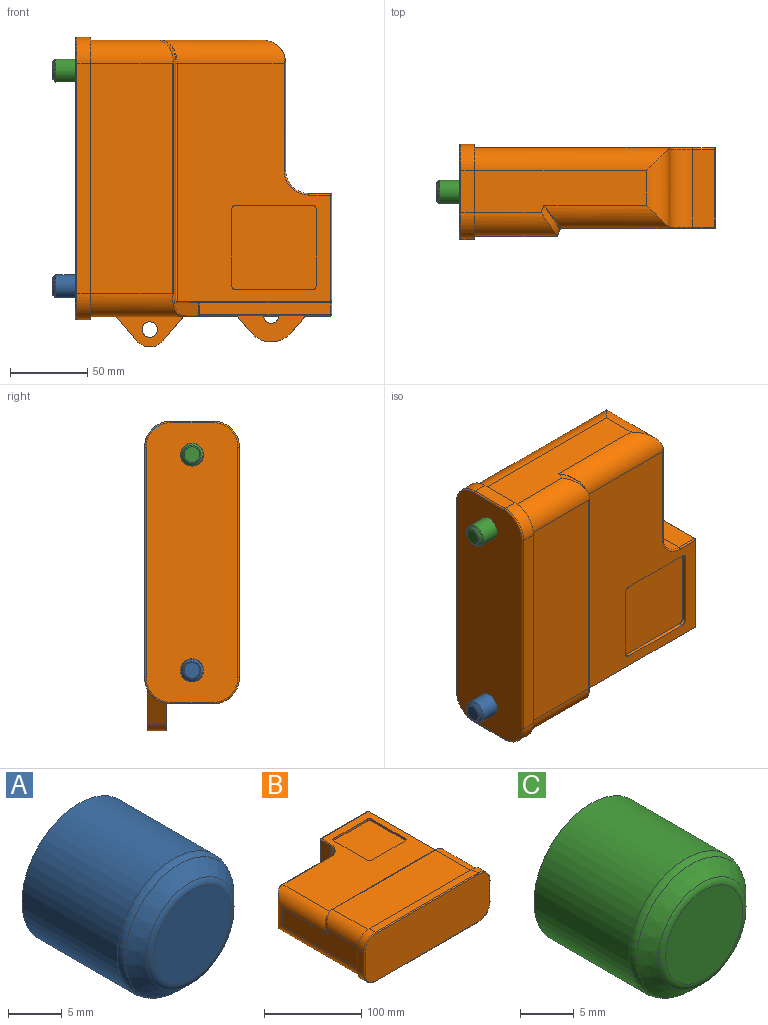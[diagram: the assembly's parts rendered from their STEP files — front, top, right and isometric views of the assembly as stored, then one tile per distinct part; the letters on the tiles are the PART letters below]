
ASSEMBLY  parts=3 mates=2
PART A: 6 faces, bbox 16.2x15x16.2 mm
  f0: cylinder r=7.5mm len=15mm, axis (0,-1,0), area 593.1mm2, adj f2,f4
  f1: plane 10.17x10.17mm, normal (0,-1,0), area 81.3mm2, adj f5
  f2: plane 15x15mm, normal (0,1,0), area 176.7mm2, adj f0
  f3: cone r=5.5mm half-angle=45deg, axis (0,1,0), area 81.7mm2, adj f4,f5
  f4: torus R=6.5mm, axis (0,-1,0), area 36.5mm2, adj f0,f3
  f5: torus R=5.09mm, axis (0,-1,0), area 26.9mm2, adj f1,f3
PART B: 131 faces, bbox 202.6x166.6x64.4 mm
  f0: cylinder r=15mm len=16.23mm, axis (0,1,0), area 221.2mm2, adj f6,f64,f67,f76
  f1: cylinder r=15mm len=95.05mm, axis (0,1,0), area 932.7mm2, adj f6,f7,f29,f61,f65,f67,f78,f81
  f2: plane 154.56x99.36mm, normal (0,0,1), area 9823.6mm2, adj f9,f16,f31,f32,f33,f34,f35,f36
  f3: plane 77.56x50.5mm, normal (0,1,0), area 3498.3mm2, adj f49,f50,f55,f59,f60,f63,f64
  f4: plane 149.5x52.92mm, normal (0,0,1), area 7911.7mm2, adj f13,f20,f29,f47
  f5: plane 111.5x27.5mm, normal (-1,0,0), area 2728.9mm2, adj f13,f14,f15,f16,f17,f29
  f6: plane 184.06x155.5mm, normal (0,0,-1), area 23247.9mm2, adj f0,f1,f15,f29,f43,f46,f51,f60
  f7: plane 68.03x27.5mm, normal (1,0,0), area 1733.1mm2, adj f1,f20,f29,f57
  f8: plane 163.5x43.68mm, normal (0,0.94,0.34), area 936.6mm2, adj f14,f47,f48,f52,f53,f57,f61,f62
  f9: plane 98.99x39mm, normal (1,0,0), area 3584mm2, adj f2,f53,f54,f55
  f10: plane 84.8x7.56mm, normal (0,0,1), area 640.7mm2, adj f54,f62,f63,f67
  f11: plane 69.5x50.5mm, normal (0,1,0), area 3509.8mm2, adj f17,f18,f40,f43
  f12: plane 50.5x14mm, normal (-1,0,0), area 707mm2, adj f18,f42,f50,f51
  f13: cylinder r=15mm len=53.49mm, axis (0,1,0), area 1172.6mm2, adj f4,f5,f14,f29,f47
  f14: cylinder r=15mm len=19.88mm, axis (0,0.34,-0.94), area 114mm2, adj f5,f8,f13,f44,f47
  f15: cylinder r=15mm len=126.21mm, axis (0,-1,0), area 2850.5mm2, adj f5,f6,f17,f29,f43
  f16: cylinder r=15mm len=81.27mm, axis (0,-1,0), area 1623.6mm2, adj f2,f5,f17,f40,f44
  f17: cylinder r=15mm len=51.91mm, axis (0,0,-1), area 976.9mm2, adj f5,f11,f15,f16,f40,f43
  f18: cylinder r=15mm len=50.5mm, axis (0,0,1), area 1189.9mm2, adj f11,f12,f41,f46
  f19: cylinder r=15mm len=10mm, axis (0,1,0), area 83.1mm2, adj f67,f79
  f20: cylinder r=15mm len=58.02mm, axis (0,-1,0), area 1290.6mm2, adj f4,f7,f29,f52
  f21: cylinder r=17mm len=17mm, axis (0,1,0), area 240.3mm2, adj f22,f28,f29,f75
  f22: plane 27.5x9mm, normal (-1,0,0), area 247.5mm2, adj f21,f23,f29,f73
  f23: cylinder r=17mm len=17mm, axis (0,1,0), area 240.3mm2, adj f22,f24,f29,f71
  f24: plane 149.5x9mm, normal (0,0,-1), area 1345.5mm2, adj f23,f25,f29,f69
  f25: cylinder r=17mm len=17mm, axis (0,1,0), area 240.3mm2, adj f24,f26,f29,f68
  f26: plane 27.5x9mm, normal (1,0,0), area 247.5mm2, adj f25,f27,f29,f70
  f27: cylinder r=17mm len=17mm, axis (0,1,0), area 240.3mm2, adj f26,f28,f29,f72
  f28: plane 149.5x9mm, normal (0,0,1), area 1345.5mm2, adj f21,f27,f29,f74
  f29: plane 183.5x61.5mm, normal (0,1,0), area 909.1mm2, adj f1,f4,f5,f6,f7,f13,f15,f20
  f30: plane 181.5x59.5mm, normal (0,-1,0), area 10579.5mm2, adj f68,f69,f70,f71,f72,f73,f74,f75
  f31: plane 49x2.5mm, normal (0,-1,0), area 122.5mm2, adj f2,f32,f38,f39
  f32: cylinder r=3mm len=3mm, axis (0,0,1), area 11.8mm2, adj f2,f31,f33,f39
  f33: plane 49x2.5mm, normal (1,0,0), area 122.5mm2, adj f2,f32,f34,f39
  f34: cylinder r=3mm len=3mm, axis (0,0,1), area 11.8mm2, adj f2,f33,f35,f39
  f35: plane 49x2.5mm, normal (0,1,0), area 122.5mm2, adj f2,f34,f36,f39
  f36: cylinder r=3mm len=3mm, axis (0,0,1), area 11.8mm2, adj f2,f35,f37,f39
  f37: plane 49x2.5mm, normal (-1,0,0), area 122.5mm2, adj f2,f36,f38,f39
  f38: cylinder r=3mm len=3mm, axis (0,0,1), area 11.8mm2, adj f2,f31,f37,f39
  f39: plane 55x55mm, normal (0,0,1), area 3017.3mm2, adj f31,f32,f33,f34,f35,f36,f37,f38
  f40: cylinder r=1mm len=72.45mm, axis (-1,0,0), area 111.5mm2, adj f2,f11,f16,f17,f41
  f41: torus R=16mm, axis (0,0,1), area 37.9mm2, adj f2,f18,f40,f42
  f42: cylinder r=1mm len=14mm, axis (0,-1,0), area 22mm2, adj f2,f12,f41,f45
  f43: cylinder r=1mm len=72.45mm, axis (1,0,0), area 111.5mm2, adj f6,f11,f15,f17,f46
  f44: bspline ~15.66x15.49mm, area 19.3mm2, adj f14,f16,f48
  f45: sphere r=1mm, area 1.6mm2, adj f42,f49,f50
  f46: torus R=16mm, axis (0,0,-1), area 37.9mm2, adj f6,f18,f43,f51
  f47: cylinder r=1mm len=151.82mm, axis (-1,0,0), area 184.1mm2, adj f4,f8,f13,f14,f52
  f48: cylinder r=1mm len=155.5mm, axis (1,0,0), area 189.3mm2, adj f2,f8,f44,f53
  f49: cylinder r=1mm len=69mm, axis (-1,0,0), area 107.8mm2, adj f2,f3,f45,f55
  f50: cylinder r=1mm len=50.5mm, axis (0,0,1), area 79.3mm2, adj f3,f12,f45,f56
  f51: cylinder r=1mm len=14mm, axis (0,1,0), area 22mm2, adj f6,f12,f46,f56
  f52: bspline ~15.65x15.01mm, area 31.9mm2, adj f8,f20,f47,f57
  f53: cylinder r=1mm len=40.34mm, axis (0,0.34,-0.94), area 65.9mm2, adj f2,f8,f9,f48,f58
  f54: cylinder r=1mm len=84.8mm, axis (0,-1,0), area 133.2mm2, adj f9,f10,f58,f59
  f55: cylinder r=1mm len=39mm, axis (0,0,1), area 60.7mm2, adj f3,f9,f49,f59
  f56: sphere r=1mm, area 1.6mm2, adj f50,f51,f60
  f57: cylinder r=1mm len=27.84mm, axis (0,-0.34,0.94), area 46mm2, adj f7,f8,f52,f61
  f58: sphere r=1mm, area 1.2mm2, adj f53,f54,f62
  f59: torus R=2mm, axis (0,1,0), area 3.4mm2, adj f3,f54,f55,f63
  f60: cylinder r=1mm len=64mm, axis (1,0,0), area 100.5mm2, adj f3,f6,f56,f64
  f61: bspline ~7.44x3.46mm, area 3.9mm2, adj f1,f8,f57,f65
  f62: cylinder r=1mm len=7.83mm, axis (1,0,0), area 9.4mm2, adj f8,f10,f58,f65
  f63: cylinder r=1mm len=7.56mm, axis (-1,0,0), area 11.9mm2, adj f3,f10,f59,f66
  f64: torus R=14mm, axis (0,1,0), area 30.3mm2, adj f0,f3,f60,f66
  f65: bspline ~2.38x2.07mm, area 2.9mm2, adj f1,f61,f62,f67
  f66: sphere r=1mm, area 1.8mm2, adj f63,f64,f67
  f67: cylinder r=1mm len=84.8mm, axis (0,1,0), area 128mm2, adj f0,f1,f10,f19,f65,f66,f76,f78
  f68: torus R=16mm, axis (0,-1,0), area 41mm2, adj f25,f30,f69,f70
  f69: cylinder r=1mm len=149.5mm, axis (-1,0,0), area 234.8mm2, adj f24,f30,f68,f71
  f70: cylinder r=1mm len=27.5mm, axis (0,0,-1), area 43.2mm2, adj f26,f30,f68,f72
  f71: torus R=16mm, axis (0,-1,0), area 41mm2, adj f23,f30,f69,f73
  f72: torus R=16mm, axis (0,-1,0), area 41mm2, adj f27,f30,f70,f74
  f73: cylinder r=1mm len=27.5mm, axis (0,0,1), area 43.2mm2, adj f22,f30,f71,f75
  f74: cylinder r=1mm len=149.5mm, axis (1,0,0), area 234.8mm2, adj f28,f30,f72,f75
  f75: torus R=16mm, axis (0,-1,0), area 41mm2, adj f21,f30,f73,f74
  f76: plane 25.37x21.39mm, normal (0.64,0.76,0), area 223.6mm2, adj f0,f6,f67,f77,f80
  f77: cylinder r=17.09mm len=26.15mm, axis (0,0,-1), area 357.2mm2, adj f6,f76,f78,f80
  f78: plane 25.37x21.39mm, normal (0.64,-0.76,0), area 223.6mm2, adj f1,f6,f67,f77,f80
  f79: cylinder r=5mm len=12mm, axis (0,0,-1), area 269.1mm2, adj f6,f19,f67,f80
  f80: plane 44.39x16.91mm, normal (0,0,1), area 454.9mm2, adj f67,f76,f77,f78,f79
  f81: plane 30.56x25.74mm, normal (0.64,-0.76,0), area 306.9mm2, adj f1,f6,f83,f85
  f82: plane 30.56x25.74mm, normal (0.64,0.76,0), area 306.9mm2, adj f1,f6,f83,f85
  f83: cylinder r=11.25mm len=17.2mm, axis (0,0,-1), area 235mm2, adj f6,f81,f82,f85
  f84: cylinder r=5mm len=12mm, axis (0,0,-1), area 377mm2, adj f6,f85
  f85: plane 43.92x19.87mm, normal (0,0,1), area 454.1mm2, adj f1,f81,f82,f83,f84
  f86: plane 169.5x47.5mm, normal (0,1,0), area 7965.4mm2, adj f94,f95,f96,f97,f103,f105,f108,f109
  f87: cylinder r=20mm len=42.5mm, axis (0,0,1), area 1309.9mm2, adj f88,f93,f96,f101,f102,f111
  f88: plane 65x62.5mm, normal (0,0,-1), area 3996.1mm2, adj f87,f89,f99,f102,f110,f111,f112,f113
  f89: plane 66.61x42.5mm, normal (0,-1,0), area 2446.6mm2, adj f88,f91,f92,f96,f99,f100,f102,f108
  f90: plane 39.07x14.24mm, normal (0,-0.94,-0.34), area 155.2mm2, adj f97,f108,f109,f118,f121
  f91: plane 5.5x2.19mm, normal (0,0,-1), area 3.8mm2, adj f89,f102,f110
  f92: plane 5.5x2.19mm, normal (0,0,-1), area 3.8mm2, adj f89,f99,f115
  f93: plane 149.87x75.69mm, normal (0,0,-1), area 7653.6mm2, adj f87,f99,f101,f106,f111,f112,f113,f114
  f94: plane 149.5x55.12mm, normal (0,0,-1), area 8240.5mm2, adj f86,f98,f103,f109
  f95: plane 116.5x27.5mm, normal (1,0,0), area 2866.4mm2, adj f86,f103,f104,f105,f106,f107
  f96: plane 175.83x156.5mm, normal (0,0,1), area 22040.2mm2, adj f86,f87,f89,f101,f102,f105,f108,f122
  f97: plane 68.77x27.5mm, normal (-1,0,0), area 1753.5mm2, adj f86,f90,f108,f109
  f98: plane 153.97x1.05mm, normal (0,-0.94,-0.34), area 170.8mm2, adj f94,f104,f109,f117
  f99: plane 93.17x34mm, normal (-1,0,0), area 2806mm2, adj f88,f89,f92,f93,f114,f115,f118,f119
  f100: plane 80.8x0.61mm, normal (0,0,-1), area 49.6mm2, adj f89,f108,f119,f121
  f101: plane 69.5x42.5mm, normal (0,-1,0), area 2953.8mm2, adj f87,f93,f96,f107
  f102: plane 42.5x10mm, normal (1,0,0), area 405.5mm2, adj f87,f88,f89,f91,f96,f110
  f103: cylinder r=10mm len=55.12mm, axis (0,1,0), area 825.9mm2, adj f86,f94,f95,f104
  f104: cylinder r=10mm len=15mm, axis (0,0.34,-0.94), area 41.6mm2, adj f95,f98,f103,f116
  f105: cylinder r=10mm len=126.5mm, axis (0,-1,0), area 1930mm2, adj f86,f95,f96,f107
  f106: cylinder r=10mm len=76.56mm, axis (0,-1,0), area 1033.5mm2, adj f93,f95,f107,f116
  f107: cylinder r=10mm len=42.5mm, axis (0,0,-1), area 553.4mm2, adj f95,f101,f105,f106
  f108: cylinder r=10mm len=156.5mm, axis (0,1,0), area 1098.7mm2, adj f86,f89,f90,f96,f97,f100,f121,f122
  f109: cylinder r=10mm len=58.76mm, axis (0,-1,0), area 886.6mm2, adj f86,f90,f94,f97,f98,f117,f118
  f110: cylinder r=8mm len=5.5mm, axis (0,0,1), area 15.2mm2, adj f88,f89,f91,f102
  f111: plane 37.32x2.5mm, normal (-1,0,0), area 93.3mm2, adj f87,f88,f93,f112
  f112: cylinder r=8mm len=8mm, axis (0,0,1), area 31.4mm2, adj f88,f93,f111,f113
  f113: plane 49x2.5mm, normal (0,-1,0), area 122.5mm2, adj f88,f93,f112,f114
  f114: cylinder r=8mm len=5.5mm, axis (0,0,1), area 15.2mm2, adj f88,f93,f99,f113
  f115: cylinder r=8mm len=5.5mm, axis (0,0,1), area 15.2mm2, adj f88,f89,f92,f99
  f116: bspline ~13.95x11.2mm, area 79.4mm2, adj f104,f106,f117
  f117: cylinder r=6mm len=154.91mm, axis (1,0,0), area 1115.7mm2, adj f93,f98,f109,f116,f118
  f118: cylinder r=6mm len=41.5mm, axis (0,0.34,-0.94), area 364.6mm2, adj f90,f93,f99,f109,f117,f120
  f119: cylinder r=6mm len=80.8mm, axis (0,-1,0), area 761.5mm2, adj f89,f99,f100,f120
  f120: sphere r=6mm, area 44mm2, adj f118,f119,f121
  f121: cylinder r=6mm len=5.64mm, axis (1,0,0), area 13mm2, adj f90,f100,f108,f120
  f122: plane 22.03x18.55mm, normal (-0.64,-0.76,0), area 46.9mm2, adj f96,f108,f123,f126
  f123: cylinder r=12.09mm len=18.5mm, axis (0,0,-1), area 42.1mm2, adj f96,f122,f124,f126
  f124: plane 22.03x18.55mm, normal (-0.64,0.76,0), area 46.9mm2, adj f96,f108,f123,f126
  f125: cylinder r=10mm len=20mm, axis (0,0,-1), area 116.8mm2, adj f96,f108,f126
  f126: plane 45.5x20.33mm, normal (0,0,-1), area 267.6mm2, adj f108,f122,f123,f124,f125
  f127: plane 21.37x17.99mm, normal (-0.64,0.76,0), area 45.2mm2, adj f96,f108,f129,f130
  f128: plane 21.37x17.99mm, normal (-0.64,-0.76,0), area 45.2mm2, adj f96,f108,f129,f130
  f129: cylinder r=10mm len=19.62mm, axis (0,0,-1), area 55mm2, adj f96,f127,f128,f130
  f130: plane 45.5x15.37mm, normal (0,0,-1), area 382mm2, adj f108,f127,f128,f129
PART C: 6 faces, bbox 16.2x15x16.2 mm
  f0: cylinder r=7.5mm len=15mm, axis (0,-1,0), area 593.1mm2, adj f2,f4
  f1: plane 10.17x10.17mm, normal (0,-1,0), area 81.3mm2, adj f5
  f2: plane 15x15mm, normal (0,1,0), area 176.7mm2, adj f0
  f3: cone r=5.5mm half-angle=45deg, axis (0,1,0), area 81.7mm2, adj f4,f5
  f4: torus R=6.5mm, axis (0,-1,0), area 36.5mm2, adj f0,f3
  f5: torus R=5.09mm, axis (0,-1,0), area 26.9mm2, adj f1,f3
PLACE A rot(axis=(0.71,0.71,0),180deg) t=(-80.86,-98.75,-54.58)mm
PLACE B rot(axis=(0.58,0.58,-0.58),120deg) t=(-80.86,-13.76,12.93)mm
PLACE C rot(axis=(0.71,0.71,0),180deg) t=(-80.86,-98.75,110.42)mm
MATE fastened A.f0 <-> B.f30  axis (1,0,0) through (-80.86,-28.75,-57.07)mm
MATE fastened C.f0 <-> B.f30  axis (1,0,0) through (-80.86,-28.75,82.93)mm
